# Revit family: 3026622D_3026622DC_NE-MAST TELESKOP 9.0-12.0M Ø76 RO240
name_source: partatom
category: Lighting Fixtures
units: mm (PartAtom-declared; Revit-internal decimal feet)

## family parameters
Always vertical = Yes
Cut with Voids When Loaded = No
Light Source = No
Maintain Annotation Orientation = No
OmniClass Number = 23.80.70.14.21
OmniClass Title = Street and Roadway Lighting
Part Type = Normal
Room Calculation Point = No
Round Connector Dimension = Use Diameter
Shared = No
Work Plane-Based = No

## types (1)
- Ettergivende master NE
    Area = 8,90 m²
    Art.nr = 3026622D/3026622DC
    Art.nr CombiCoat = 3026622DC
    Art.nr VZN = 3026622D
    Bunndiameter = Ø140
    CE-godkjent = Ja
    Category = Ettergivende master NE
    Center of Gravity = X: -0,002 mm Y: 1,191 mm Z: 5405,925 mm
    Default Elevation = 0 mm  [stored 0 ft]
    Density = 7803,55 kg/m³
    Description = NE-MAST TELESKOP 9.0-12.0M Ø76 RO240
    Design Status = 1
    Designer = khk
    EL nr CombiCoat = 3641212
    El nr = 3640106/3640118
    El nr VZN = 3641211
    Filnamn-VO = Standard
    Filnavn = NE-MAST TELESKOP 9.0-12.0M Ø76 RO240
    Fotplate C/C bolter = 240RO
    Fundament = Fotplate
    Lyspunkthoyde = 9-12m
    Manufacturer = Vik Ørsta AS
    Mass = 133,40 kg
    Model = 3026622D_3026622DC
    Part Number = L10221
    Requested Accuracy = Low
    Revision Number = -
    Size = 0,0,0
    Sti&Filnamn-VO = Standard
    Title = NE-MAST TELESKOP 9.0-12.0M Ø76 RO240
    Toppdiameter = Ø76
    Volume = 0,02 m³

note: [stored X ft] marks values corroborated as IEEE doubles in the binary element streams (Revit-internal decimal feet)

## geometry (parser evidence)
native form markers: Sweep x3
no freeform markers — native parametric forms only
